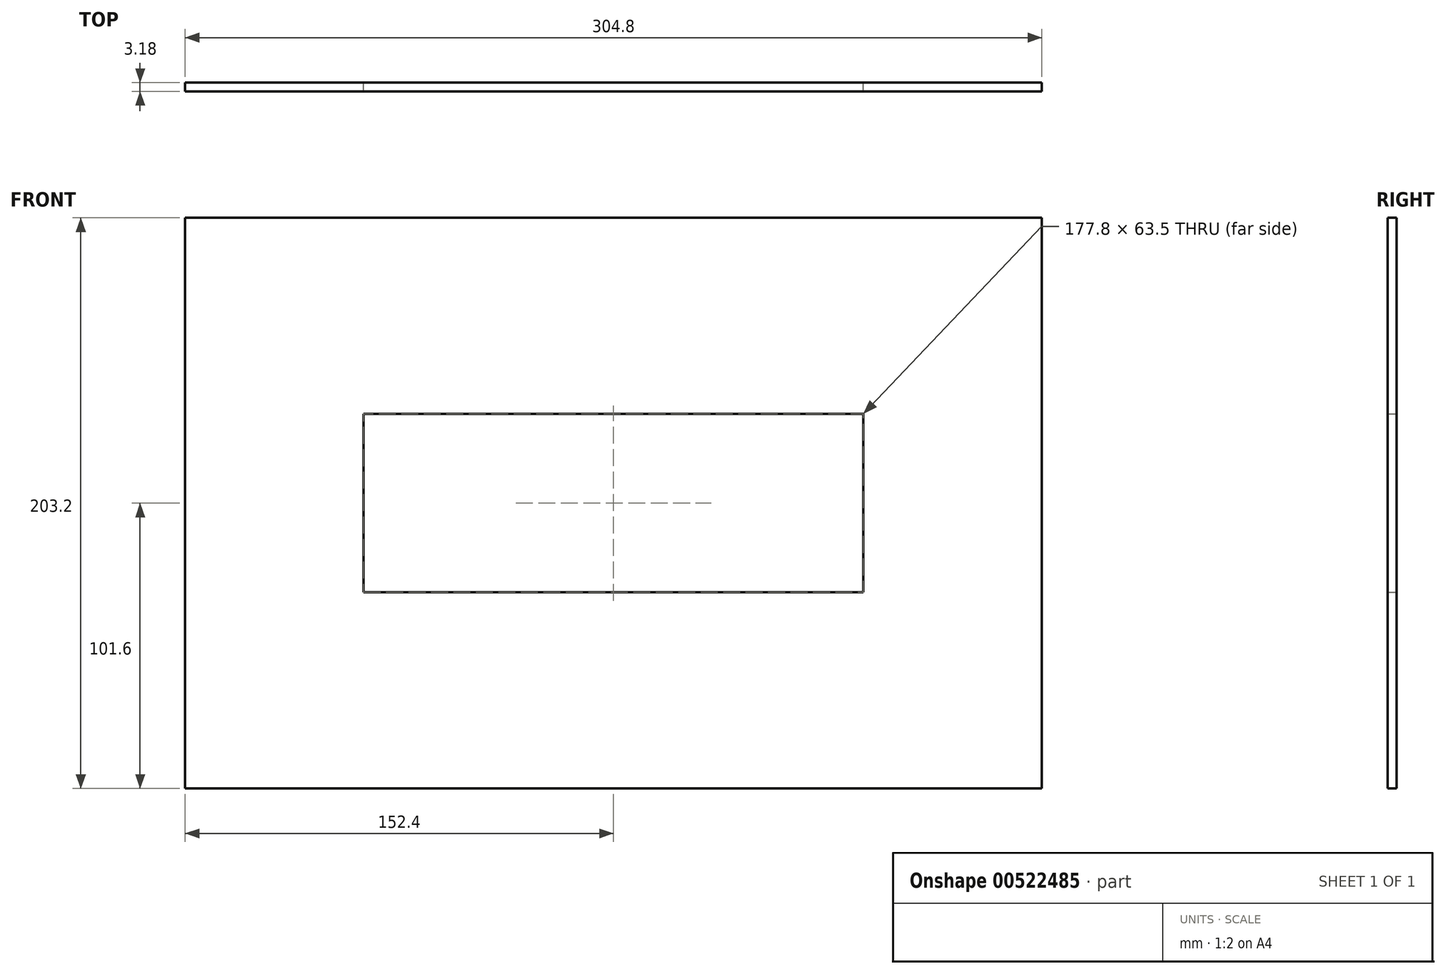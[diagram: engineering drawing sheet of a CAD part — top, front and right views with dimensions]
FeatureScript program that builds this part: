
annotation { "Feature Type Name" : "Feature", "Feature Type Description" : "" }
export const myFeature = defineFeature(function(context is Context, id is Id, definition is map)
    precondition{}
    {
        {
            var Q0;
            Q0=qCreatedBy(makeId("Front.planeOp"),FACE);
            var sketch = newSketch(context, id + "F0", { "sketchPlane" : qUnion([Q0])});
            skLineSegment(sketch, "E0.bottom", {"start": v(-152.4, 101.6) * mm, "end": v(152.4, 101.6) * mm});
            skLineSegment(sketch, "E0.top", {"start": v(-152.4, -101.6) * mm, "end": v(152.4, -101.6) * mm});
            skLineSegment(sketch, "E0.left", {"start": v(-152.4, 101.6) * mm, "end": v(-152.4, -101.6) * mm});
            skLineSegment(sketch, "E0.right", {"start": v(152.4, 101.6) * mm, "end": v(152.4, -101.6) * mm});
            skPoint(sketch, "E0.middle", {"position": v(0, 0) * mm});
            skSolve(sketch);
        }
        {
            var Q0;
            Q0=makeQuery(id+"F0.imprint","IMPRINT",FACE,{"disambiguationData":[TD([[makeQuery(id+"F0.imprint","IMPRINT",EDGE,{"derivedFrom":sQuery(id+"F0.wireOp",EDGE,"E0.bottom")}),-1.0]])]});
            extrude(context, id + "F1", {"entities" : qUnion([Q0]), "depth" : 3.17 * mm, "offsetDistance" : 25.4 * mm});
        }
        {
            var Q0;
            Q0=makeQuery(id+"F1.opExtrude","CAP_FACE",FACE,{"disambiguationData":[OSD([sQuery(id+"F0.wireOp",EDGE,"E0.bottom"),sQuery(id+"F0.wireOp",EDGE,"E0.top"),sQuery(id+"F0.wireOp",EDGE,"E0.left"),sQuery(id+"F0.wireOp",EDGE,"E0.right")])],"isStart":true});
            var sketch = newSketch(context, id + "F2", { "sketchPlane" : qUnion([Q0])});
            skLineSegment(sketch, "E1.bottom", {"start": v(-88.9, 31.75) * mm, "end": v(88.9, 31.75) * mm});
            skLineSegment(sketch, "E1.top", {"start": v(-88.9, -31.75) * mm, "end": v(88.9, -31.75) * mm});
            skLineSegment(sketch, "E1.left", {"start": v(-88.9, 31.75) * mm, "end": v(-88.9, -31.75) * mm});
            skLineSegment(sketch, "E1.right", {"start": v(88.9, 31.75) * mm, "end": v(88.9, -31.75) * mm});
            skPoint(sketch, "E1.middle", {"position": v(0, 0) * mm});
            skSolve(sketch);
        }
        {
            var Q0;
            Q0=makeQuery(id+"F2.imprint","IMPRINT",FACE,{"disambiguationData":[TD([[makeQuery(id+"F2.imprint","IMPRINT",EDGE,{"derivedFrom":sQuery(id+"F2.wireOp",EDGE,"E1.bottom")}),-1.0]])]});
            extrude(context, id + "F3", {"entities" : qUnion([Q0]), "operationType" : NewBodyOperationType.REMOVE, "endBound" : BoundingType.SYMMETRIC, "oppositeDirection" : true, "depth" : 25.4 * mm, "offsetDistance" : 25.4 * mm});
        }
    });
